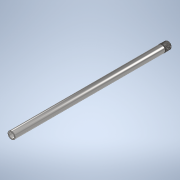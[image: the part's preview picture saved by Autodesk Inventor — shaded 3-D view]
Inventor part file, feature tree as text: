
AUTODESK INVENTOR PART (.ipt)
format: ipt  version: 2022 (Build 260153000, 153)  size: 812,032 bytes
history: native  units: in
note: dims shown in document units (in); Inventor stores cm internally (conversion verified against a paired STEP export)
features: extrude x1, sketch x1, revolve x1
ambient origin geometry x8: Origin, YZ Plane, XZ Plane, XY Plane, X Axis, Y Axis, Z Axis, Center Point
bodies: Solid1 (feature_tree)
feature tree (3):
  extrude  "Extrusion1"  [1 undecoded]
  sketch  "Sketch1"  dims[d0=12.0in d1=0.0in]
  revolve  "Revolve2"  [1 undecoded]
note: 2 required parameter values undecoded (feature->parameter linkage not recoverable at this tier; creation-order binding heuristic only, values carry confidence <= 0.55)
